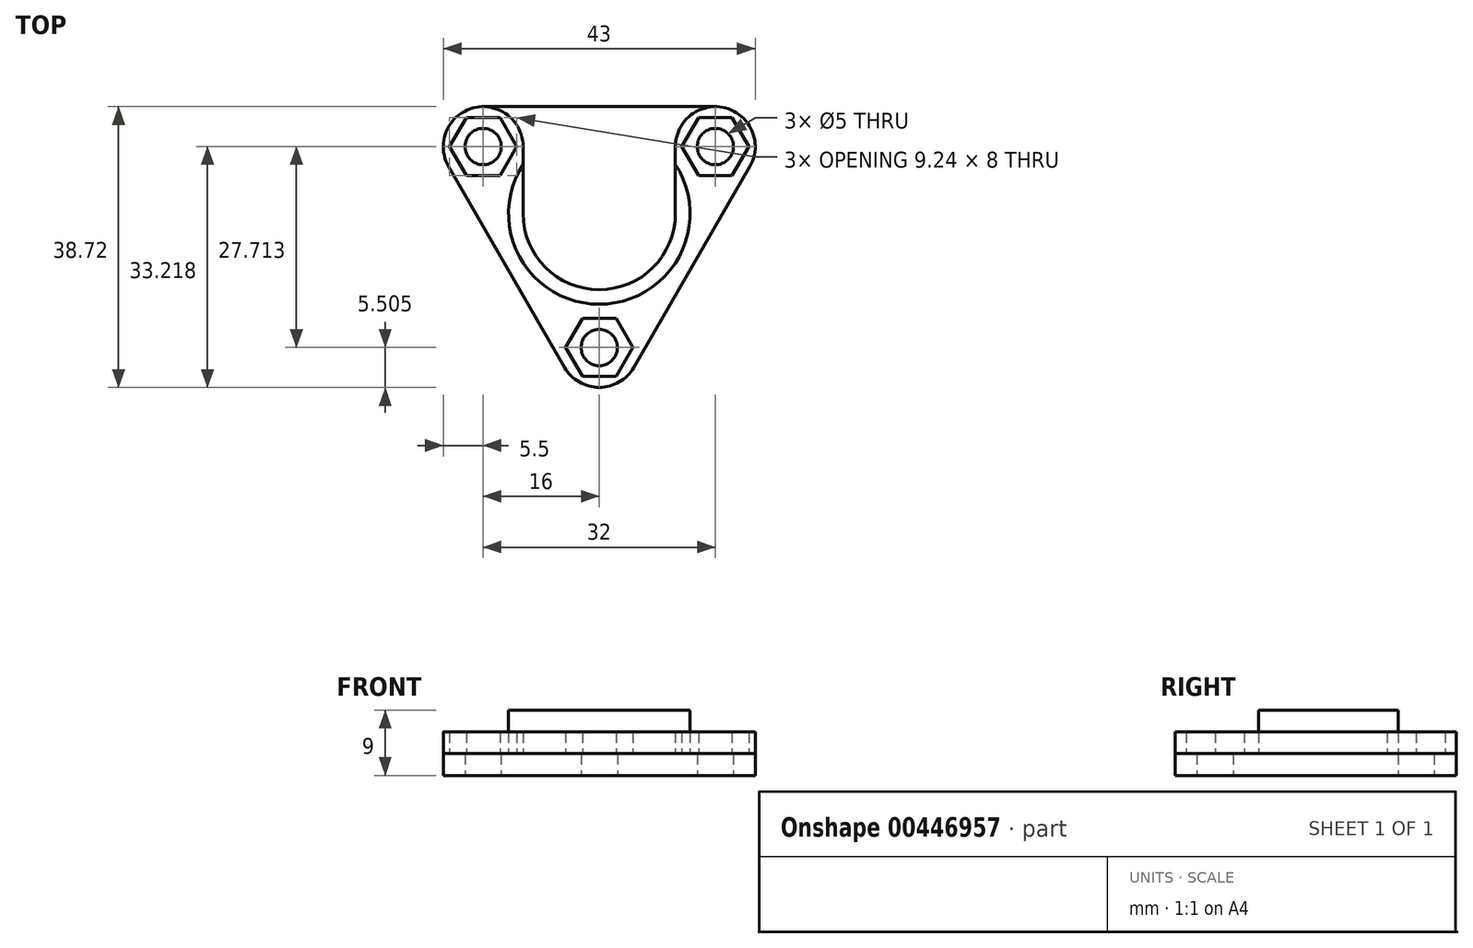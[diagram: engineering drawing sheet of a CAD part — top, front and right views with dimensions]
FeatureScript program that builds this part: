
annotation { "Feature Type Name" : "Feature", "Feature Type Description" : "" }
export const myFeature = defineFeature(function(context is Context, id is Id, definition is map)
    precondition{}
    {
        {
            var Q0;
            Q0=qCreatedBy(makeId("Top.planeOp"),FACE);
            var sketch = newSketch(context, id + "F0", { "sketchPlane" : qUnion([Q0])});
            skCircle(sketch, "E0", {"center": v(0, 0) * mm, "radius": 10.5 * mm});
            skCircle(sketch, "E1", {"center": v(0, 0) * mm, "radius": 12.5 * mm});
            skLineSegment(sketch, "E2", {"start": v(-16, 14.74) * mm, "end": v(16, 14.74) * mm});
            skLineSegment(sketch, "E3", {"start": v(-20.76, 6.49) * mm, "end": v(-4.76, -21.23) * mm});
            skLineSegment(sketch, "E4", {"start": v(4.76, -21.23) * mm, "end": v(20.76, 6.49) * mm});
            skCircle(sketch, "E5", {"center": v(-16, 9.24) * mm, "radius": 5.5 * mm});
            skCircle(sketch, "E6", {"center": v(16, 9.24) * mm, "radius": 5.5 * mm});
            skCircle(sketch, "E7", {"center": v(0, -18.48) * mm, "radius": 5.5 * mm});
            skCircle(sketch, "E8.cCircle", {"center": v(16, 9.24) * mm, "radius": 4 * mm, "construction": true});
            skLineSegment(sketch, "E8.0", {"start": v(13.7, 13.24) * mm, "end": v(18.3, 13.24) * mm});
            skLineSegment(sketch, "E8.1", {"start": v(18.3, 13.24) * mm, "end": v(20.62, 9.24) * mm});
            skLineSegment(sketch, "E8.2", {"start": v(20.62, 9.24) * mm, "end": v(18.3, 5.24) * mm});
            skLineSegment(sketch, "E8.3", {"start": v(18.3, 5.24) * mm, "end": v(13.7, 5.24) * mm});
            skLineSegment(sketch, "E8.4", {"start": v(13.7, 5.24) * mm, "end": v(11.38, 9.24) * mm});
            skLineSegment(sketch, "E8.5", {"start": v(11.38, 9.24) * mm, "end": v(13.7, 13.24) * mm});
            skPoint(sketch, "E8.0.midPoint", {"position": v(16, 13.24) * mm});
            skLineSegment(sketch, "E9", {"start": v(-16, 9.24) * mm, "end": v(0, 0) * mm, "construction": true});
            skLineSegment(sketch, "E10", {"start": v(0, -18.48) * mm, "end": v(0, 0) * mm, "construction": true});
            skLineSegment(sketch, "E11.1.0", {"start": v(-13.7, 13.24) * mm, "end": v(-11.38, 9.24) * mm});
            skLineSegment(sketch, "E11.1.1", {"start": v(-11.38, 9.24) * mm, "end": v(-13.7, 5.24) * mm});
            skLineSegment(sketch, "E11.1.2", {"start": v(-18.3, 13.24) * mm, "end": v(-13.7, 13.24) * mm});
            skLineSegment(sketch, "E11.1.3", {"start": v(-20.62, 9.24) * mm, "end": v(-18.3, 13.24) * mm});
            skLineSegment(sketch, "E11.1.4", {"start": v(-18.3, 5.24) * mm, "end": v(-20.62, 9.24) * mm});
            skLineSegment(sketch, "E11.1.5", {"start": v(-13.7, 5.24) * mm, "end": v(-18.3, 5.24) * mm});
            skLineSegment(sketch, "E11.2.0", {"start": v(-4.62, -18.48) * mm, "end": v(-2.3, -14.48) * mm});
            skLineSegment(sketch, "E11.2.1", {"start": v(-2.3, -14.48) * mm, "end": v(2.3, -14.48) * mm});
            skLineSegment(sketch, "E11.2.2", {"start": v(-2.3, -22.48) * mm, "end": v(-4.62, -18.48) * mm});
            skLineSegment(sketch, "E11.2.3", {"start": v(2.3, -22.48) * mm, "end": v(-2.3, -22.48) * mm});
            skLineSegment(sketch, "E11.2.4", {"start": v(4.62, -18.48) * mm, "end": v(2.3, -22.48) * mm});
            skLineSegment(sketch, "E11.2.5", {"start": v(2.3, -14.48) * mm, "end": v(4.62, -18.48) * mm});
            skLineSegment(sketch, "E12", {"start": v(10.5, 0) * mm, "end": v(10.5, 14.74) * mm});
            skLineSegment(sketch, "E13", {"start": v(-10.5, 0) * mm, "end": v(-10.5, 14.74) * mm});
            skCircle(sketch, "E14", {"center": v(16, 9.24) * mm, "radius": 2.5 * mm});
            skCircle(sketch, "E15", {"center": v(-16, 9.24) * mm, "radius": 2.5 * mm});
            skCircle(sketch, "E16", {"center": v(0, -18.48) * mm, "radius": 2.5 * mm});
            skSolve(sketch);
        }
        {
            var Q0;
            {var subQ5=sQuery(id+"F0.wireOp",EDGE,"E3");Q0=makeQuery(id+"F0.imprint","IMPRINT",FACE,{"disambiguationData":[TD([[makeQuery(id+"F0.imprint","IMPRINT",EDGE,{"derivedFrom":subQ5}),1.0]])]});}
            var Q1;
            {var subQ0=sQuery(id+"F0.wireOp",EDGE,"E12");var subQ1=sQuery(id+"F0.wireOp",EDGE,"E1");var subQ2=makeQuery(id+"F0.imprint","INTERSECT",VERTEX,{"derivedFrom":[subQ1,subQ0]});Q1=makeQuery(id+"F0.imprint","IMPRINT",FACE,{"disambiguationData":[TD([[makeQuery(id+"F0.imprint","IMPRINT",EDGE,{"disambiguationData":[TD([[subQ2,-1.0]])],"derivedFrom":subQ1}),1.0]])]});}
            var Q2;
            {var subQ0=sQuery(id+"F0.wireOp",EDGE,"E12");var subQ1=sQuery(id+"F0.wireOp",EDGE,"E1");var subQ2=makeQuery(id+"F0.imprint","INTERSECT",VERTEX,{"derivedFrom":[subQ1,subQ0]});Q2=makeQuery(id+"F0.imprint","IMPRINT",FACE,{"disambiguationData":[TD([[makeQuery(id+"F0.imprint","IMPRINT",EDGE,{"disambiguationData":[TD([[subQ2,1.0]])],"derivedFrom":subQ1}),1.0]])]});}
            var Q3;
            {var subQ1=sQuery(id+"F0.wireOp",EDGE,"E8.0");Q3=makeQuery(id+"F0.imprint","IMPRINT",FACE,{"disambiguationData":[TD([[makeQuery(id+"F0.imprint","IMPRINT",EDGE,{"derivedFrom":subQ1}),-1.0]])]});}
            var Q4;
            {var subQ0=sQuery(id+"F0.wireOp",EDGE,"E6");var subQ1=sQuery(id+"F0.wireOp",EDGE,"E2");var subQ2=makeQuery(id+"F0.imprint","INTERSECT",VERTEX,{"derivedFrom":[subQ1,subQ0]});Q4=makeQuery(id+"F0.imprint","IMPRINT",FACE,{"disambiguationData":[TD([[makeQuery(id+"F0.imprint","IMPRINT",EDGE,{"disambiguationData":[TD([[subQ2,1.0]])],"derivedFrom":subQ1}),-1.0]])]});}
            var Q5;
            {var subQ0=sQuery(id+"F0.wireOp",EDGE,"E7");var subQ1=sQuery(id+"F0.wireOp",EDGE,"E1");var subQ2=makeQuery(id+"F0.imprint","INTERSECT",VERTEX,{"disambiguationData":[OD(0.0)],"derivedFrom":[subQ1,subQ0]});Q5=makeQuery(id+"F0.imprint","IMPRINT",FACE,{"disambiguationData":[TD([[makeQuery(id+"F0.imprint","IMPRINT",EDGE,{"disambiguationData":[TD([[subQ2,-1.0]])],"derivedFrom":subQ1}),1.0]])]});}
            var Q6;
            {var subQ0=sQuery(id+"F0.wireOp",EDGE,"E5");var subQ1=sQuery(id+"F0.wireOp",EDGE,"E1");var subQ2=makeQuery(id+"F0.imprint","INTERSECT",VERTEX,{"disambiguationData":[OD(0.0)],"derivedFrom":[subQ1,subQ0]});Q6=makeQuery(id+"F0.imprint","IMPRINT",FACE,{"disambiguationData":[TD([[makeQuery(id+"F0.imprint","IMPRINT",EDGE,{"disambiguationData":[TD([[subQ2,-1.0]])],"derivedFrom":subQ1}),1.0]])]});}
            var Q7;
            Q7=makeQuery(id+"F0.imprint","IMPRINT",FACE,{"disambiguationData":[TD([[makeQuery(id+"F0.imprint","IMPRINT",EDGE,{"derivedFrom":sQuery(id+"F0.wireOp",EDGE,"E11.2.0")}),-1.0]])]});
            var Q8;
            Q8=makeQuery(id+"F0.imprint","IMPRINT",FACE,{"disambiguationData":[TD([[makeQuery(id+"F0.imprint","IMPRINT",EDGE,{"derivedFrom":sQuery(id+"F0.wireOp",EDGE,"E11.1.0")}),-1.0]])]});
            var Q9;
            Q9=makeQuery(id+"F0.imprint","IMPRINT",FACE,{"disambiguationData":[TD([[makeQuery(id+"F0.imprint","IMPRINT",EDGE,{"derivedFrom":sQuery(id+"F0.wireOp",EDGE,"E0")}),1.0]])]});
            var Q10;
            {var subQ1=sQuery(id+"F0.wireOp",EDGE,"E8.0");Q10=makeQuery(id+"F0.imprint","IMPRINT",FACE,{"disambiguationData":[TD([[makeQuery(id+"F0.imprint","IMPRINT",EDGE,{"derivedFrom":subQ1}),1.0]])]});}
            var Q11;
            Q11=makeQuery(id+"F0.imprint","IMPRINT",FACE,{"disambiguationData":[TD([[makeQuery(id+"F0.imprint","IMPRINT",EDGE,{"derivedFrom":sQuery(id+"F0.wireOp",EDGE,"E11.1.0")}),1.0]])]});
            var Q12;
            {var subQ0=sQuery(id+"F0.wireOp",EDGE,"E6");var subQ1=sQuery(id+"F0.wireOp",EDGE,"E1");var subQ2=makeQuery(id+"F0.imprint","INTERSECT",VERTEX,{"disambiguationData":[OD(1.0)],"derivedFrom":[subQ1,subQ0]});Q12=makeQuery(id+"F0.imprint","IMPRINT",FACE,{"disambiguationData":[TD([[makeQuery(id+"F0.imprint","IMPRINT",EDGE,{"disambiguationData":[TD([[subQ2,-1.0]])],"derivedFrom":subQ1}),-1.0]])]});}
            var Q13;
            {var subQ3=sQuery(id+"F0.wireOp",EDGE,"E12");var subQ7=sQuery(id+"F0.wireOp",EDGE,"E1");var subQ10=makeQuery(id+"F0.imprint","INTERSECT",VERTEX,{"derivedFrom":[subQ7,subQ3]});Q13=makeQuery(id+"F0.imprint","IMPRINT",FACE,{"disambiguationData":[TD([[makeQuery(id+"F0.imprint","IMPRINT",EDGE,{"disambiguationData":[TD([[subQ10,-1.0]])],"derivedFrom":subQ7}),-1.0]])]});}
            var Q14;
            Q14=makeQuery(id+"F0.imprint","IMPRINT",FACE,{"disambiguationData":[TD([[makeQuery(id+"F0.imprint","IMPRINT",EDGE,{"derivedFrom":sQuery(id+"F0.wireOp",EDGE,"E11.2.0")}),1.0]])]});
            var Q15;
            {var subQ5=sQuery(id+"F0.wireOp",EDGE,"E4");Q15=makeQuery(id+"F0.imprint","IMPRINT",FACE,{"disambiguationData":[TD([[makeQuery(id+"F0.imprint","IMPRINT",EDGE,{"derivedFrom":subQ5}),1.0]])]});}
            var Q16;
            Q16=makeQuery(id+"F0.imprint","IMPRINT",FACE,{"disambiguationData":[TD([[makeQuery(id+"F0.imprint","IMPRINT",EDGE,{"derivedFrom":sQuery(id+"F0.wireOp",EDGE,"E0")}),-1.0]])]});
            var Q17;
            {var subQ0=sQuery(id+"F0.wireOp",EDGE,"E8.5");var subQ1=sQuery(id+"F0.wireOp",EDGE,"E8.4");var subQ2=makeQuery(id+"F0.imprint","INTERSECT",VERTEX,{"derivedFrom":[subQ1,subQ0]});Q17=makeQuery(id+"F0.imprint","IMPRINT",FACE,{"disambiguationData":[TD([[makeQuery(id+"F0.imprint","IMPRINT",EDGE,{"disambiguationData":[TD([[subQ2,1.0]])],"derivedFrom":subQ1}),-1.0]])]});}
            var Q18;
            {var subQ0=sQuery(id+"F0.wireOp",EDGE,"E5");var subQ1=sQuery(id+"F0.wireOp",EDGE,"E2");var subQ2=makeQuery(id+"F0.imprint","INTERSECT",VERTEX,{"derivedFrom":[subQ1,subQ0]});Q18=makeQuery(id+"F0.imprint","IMPRINT",FACE,{"disambiguationData":[TD([[makeQuery(id+"F0.imprint","IMPRINT",EDGE,{"disambiguationData":[TD([[subQ2,-1.0]])],"derivedFrom":subQ1}),-1.0]])]});}
            extrude(context, id + "F1", {"entities" : qUnion([Q0, Q1, Q2, Q3, Q4, Q5, Q6, Q7, Q8, Q9, Q10, Q11, Q12, Q13, Q14, Q15, Q16, Q17, Q18]), "depth" : 3 * mm});
        }
        {
            var Q0;
            Q0=makeQuery(id+"F0.imprint","IMPRINT",FACE,{"disambiguationData":[TD([[makeQuery(id+"F0.imprint","IMPRINT",EDGE,{"derivedFrom":sQuery(id+"F0.wireOp",EDGE,"E11.1.0")}),1.0]])]});
            var Q1;
            Q1=makeQuery(id+"F0.imprint","IMPRINT",FACE,{"disambiguationData":[TD([[makeQuery(id+"F0.imprint","IMPRINT",EDGE,{"derivedFrom":sQuery(id+"F0.wireOp",EDGE,"E11.2.0")}),1.0]])]});
            var Q2;
            {var subQ1=sQuery(id+"F0.wireOp",EDGE,"E8.0");Q2=makeQuery(id+"F0.imprint","IMPRINT",FACE,{"disambiguationData":[TD([[makeQuery(id+"F0.imprint","IMPRINT",EDGE,{"derivedFrom":subQ1}),1.0]])]});}
            var Q3;
            {var subQ1=sQuery(id+"F0.wireOp",EDGE,"E3");Q3=makeQuery(id+"F0.imprint","IMPRINT",FACE,{"disambiguationData":[TD([[makeQuery(id+"F0.imprint","IMPRINT",EDGE,{"derivedFrom":subQ1}),1.0]])]});}
            extrude(context, id + "F2", {"entities" : qUnion([Q0, Q1, Q2, Q3]), "depth" : 6 * mm, "hasSecondDirection" : true, "secondDirectionOppositeDirection" : true, "secondDirectionDepth" : -3 * mm});
        }
        {
            var Q0;
            {var subQ0=sQuery(id+"F0.wireOp",EDGE,"E12");var subQ1=sQuery(id+"F0.wireOp",EDGE,"E0");var subQ2=makeQuery(id+"F0.imprint","INTERSECT",VERTEX,{"derivedFrom":[subQ1,subQ0]});Q0=makeQuery(id+"F0.imprint","IMPRINT",FACE,{"disambiguationData":[TD([[makeQuery(id+"F0.imprint","IMPRINT",EDGE,{"disambiguationData":[TD([[subQ2,1.0]])],"derivedFrom":subQ1}),-1.0]])]});}
            extrude(context, id + "F3", {"entities" : qUnion([Q0]), "depth" : 9 * mm, "hasSecondDirection" : true, "secondDirectionOppositeDirection" : true, "secondDirectionDepth" : -3 * mm});
        }
    });
